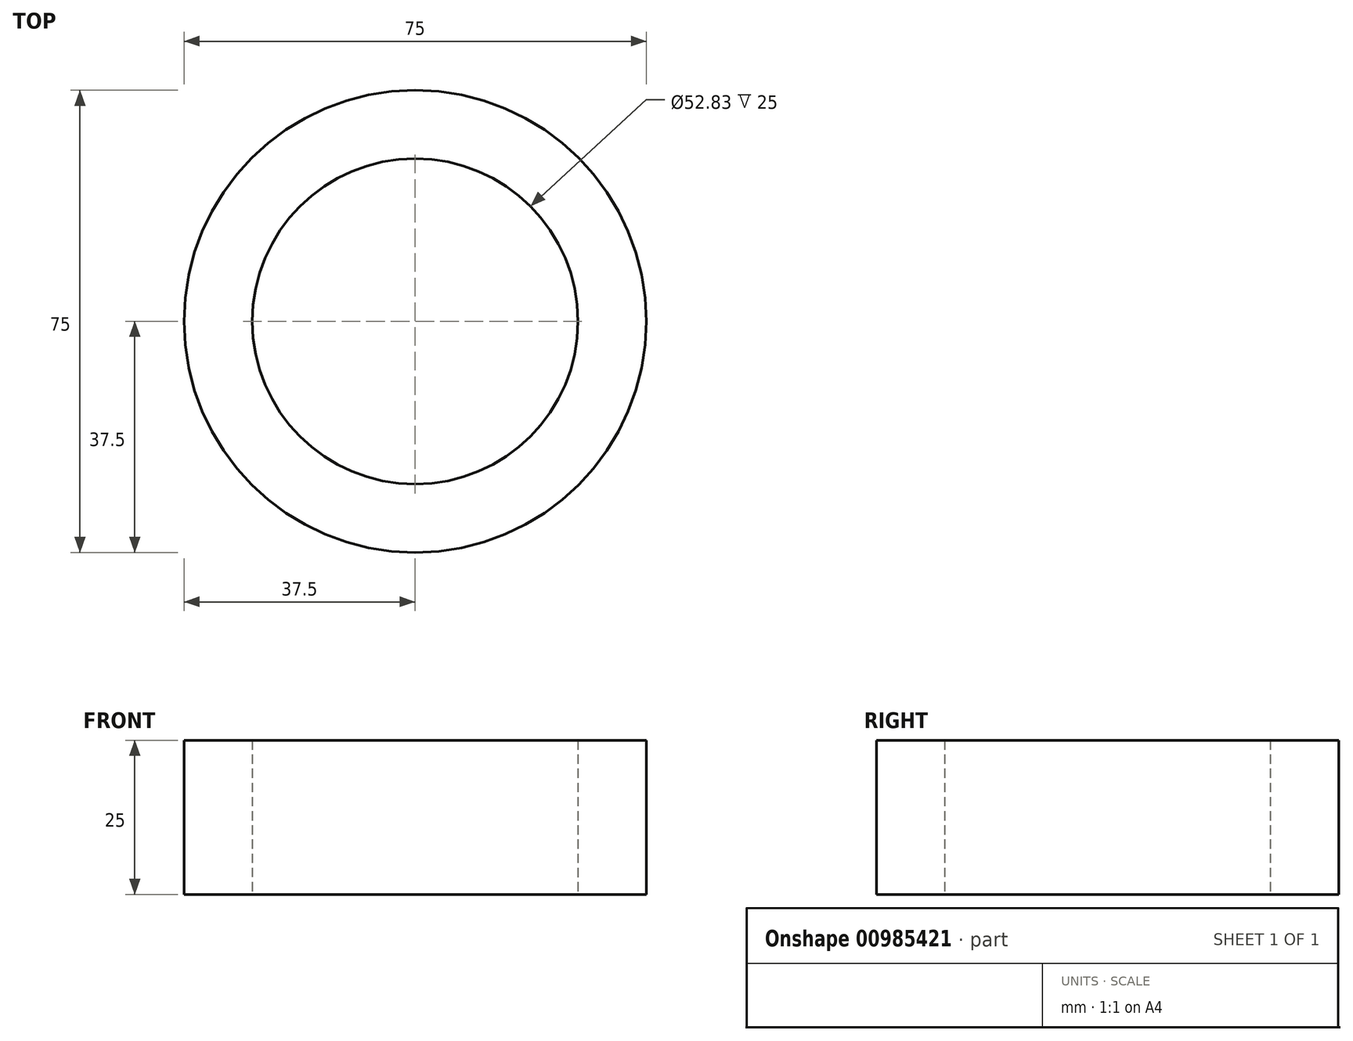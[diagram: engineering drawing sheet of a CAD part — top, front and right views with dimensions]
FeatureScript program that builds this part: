
annotation { "Feature Type Name" : "Feature", "Feature Type Description" : "" }
export const myFeature = defineFeature(function(context is Context, id is Id, definition is map)
    precondition{}
    {
        {
            var Q0;
            Q0=qCreatedBy(makeId("Top.planeOp"),FACE);
            var sketch = newSketch(context, id + "F0", { "sketchPlane" : qUnion([Q0])});
            skCircle(sketch, "E0", {"center": v(0, 0) * mm, "radius": 26.42 * mm});
            skCircle(sketch, "E1", {"center": v(0, 0) * mm, "radius": 37.5 * mm});
            skSolve(sketch);
        }
        {
            var Q0;
            Q0 = qSketchRegion(id + "F0", true);
            extrude(context, id + "F1", {"entities" : qUnion([Q0]), "depth" : 25 * mm, "offsetDistance" : 25 * mm});
        }
    });
